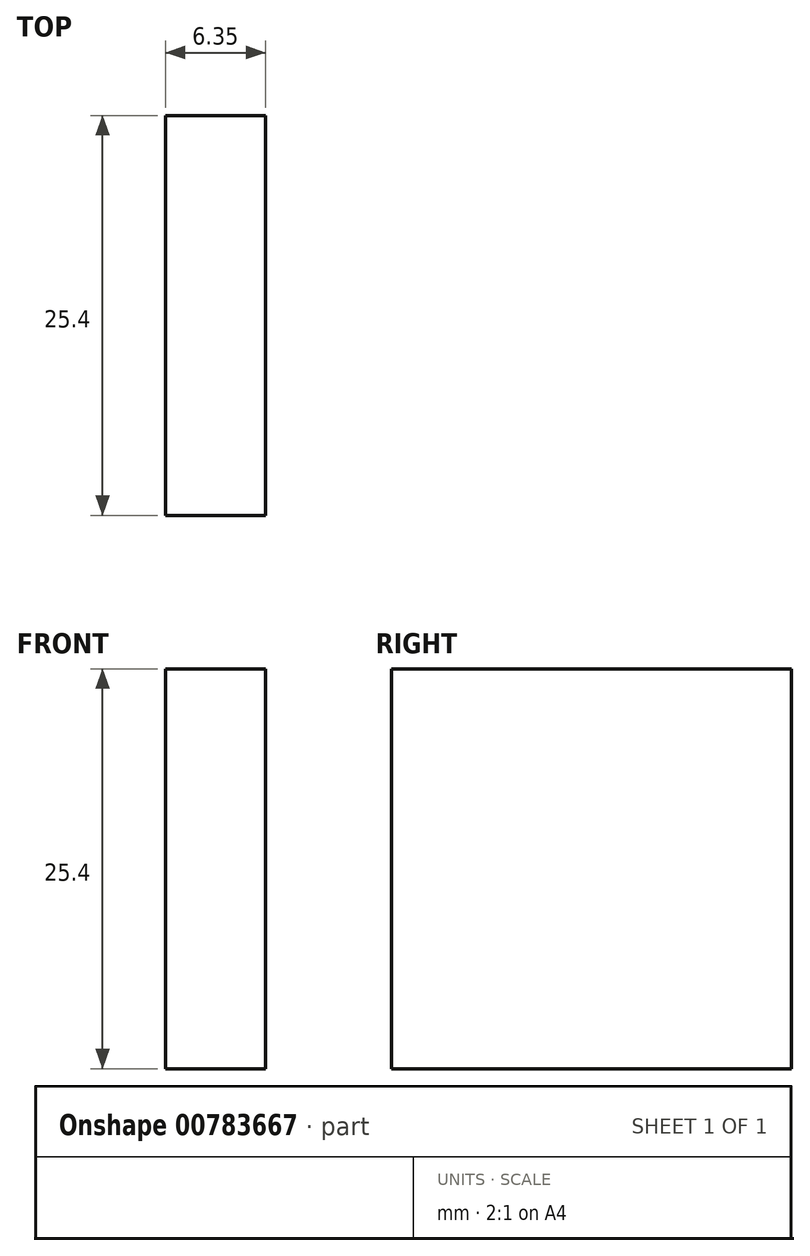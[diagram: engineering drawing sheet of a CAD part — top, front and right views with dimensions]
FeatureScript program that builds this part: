
annotation { "Feature Type Name" : "Feature", "Feature Type Description" : "" }
export const myFeature = defineFeature(function(context is Context, id is Id, definition is map)
    precondition{}
    {
        {
            var Q0;
            Q0=qCreatedBy(makeId("Right.planeOp"),FACE);
            var sketch = newSketch(context, id + "F0", { "sketchPlane" : qUnion([Q0])});
            skLineSegment(sketch, "E0", {"start": v(0, 0) * mm, "end": v(0, 25.4) * mm});
            skLineSegment(sketch, "E1", {"start": v(0, 25.4) * mm, "end": v(25.4, 25.4) * mm});
            skLineSegment(sketch, "E2", {"start": v(25.4, 25.4) * mm, "end": v(25.4, 0) * mm});
            skLineSegment(sketch, "E3", {"start": v(25.4, 0) * mm, "end": v(0, 0) * mm});
            skSolve(sketch);
        }
        {
            var Q0;
            Q0 = qSketchRegion(id + "F0", true);
            extrude(context, id + "F1", {"entities" : qUnion([Q0]), "depth" : 6.35 * mm, "offsetDistance" : 25.4 * mm});
        }
    });
